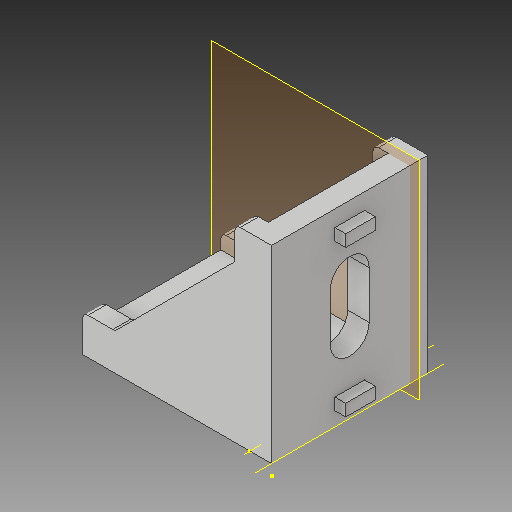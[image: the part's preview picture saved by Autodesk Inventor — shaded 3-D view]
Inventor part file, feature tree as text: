
AUTODESK INVENTOR PART (.ipt)
format: ipt  version: 2017 (Build 210142000, 142)  size: 181,248 bytes
history: native  units: mm
features: sketch x8, other x5, plane x1
ambient origin geometry x8: Origin, YZ Plane, XZ Plane, XY Plane, X Axis, Y Axis, Z Axis, Center Point
bodies: Solid1 (feature_tree)
feature tree (14):
  other  "30mm Bracket_CPY_MIR2_MIR.ipt"
  other  "Solid1::30mm Bracket_CPY_MIR2_MIR.ipt"
  other  "TaggingFeature1"
  sketch  "Sketch1"  dims[d0=10.0mm]
  sketch  "Sketch2"
  sketch  "Sketch3"
  sketch  "Sketch4"
  sketch  "Sketch5"
  sketch  "Sketch7"
  sketch  "Sketch9"
  sketch  "Sketch10"
  plane  "Work Plane1"
  other  "Work Axis1"
  other  "Work Axis2"
